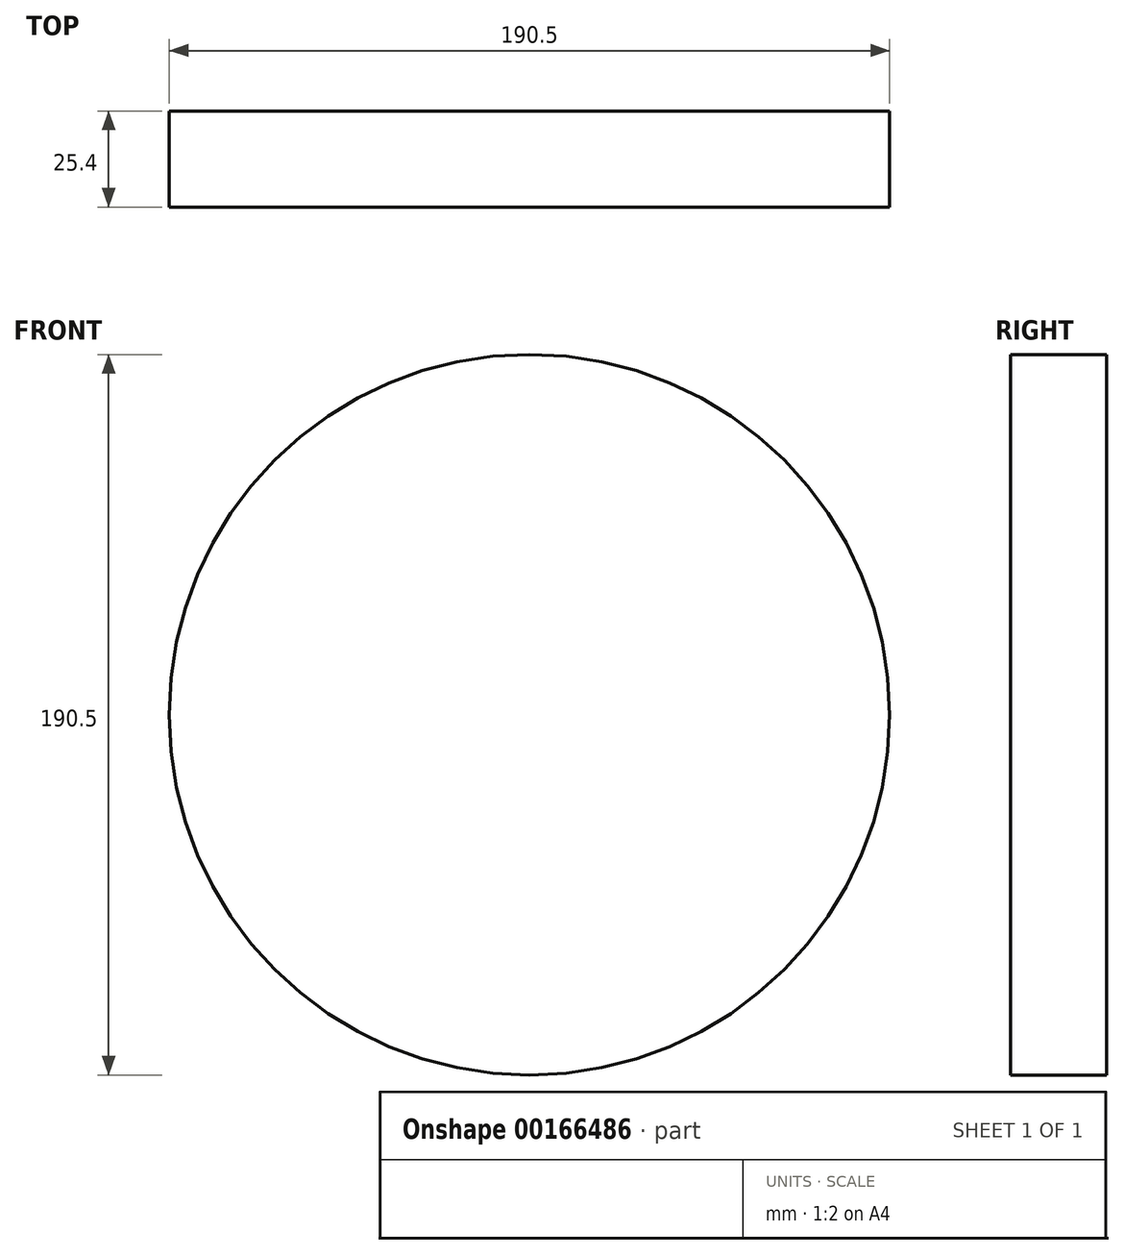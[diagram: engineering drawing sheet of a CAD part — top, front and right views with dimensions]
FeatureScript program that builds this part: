
annotation { "Feature Type Name" : "Feature", "Feature Type Description" : "" }
export const myFeature = defineFeature(function(context is Context, id is Id, definition is map)
    precondition{}
    {
        {
            var Q0;
            Q0=qCreatedBy(makeId("Front.planeOp"),FACE);
            var sketch = newSketch(context, id + "F0", { "sketchPlane" : qUnion([Q0])});
            skCircle(sketch, "E0", {"center": v(0, 0) * mm, "radius": 95.25 * mm});
            skSolve(sketch);
        }
        {
            var Q0;
            Q0 = qSketchRegion(id + "F0", true);
            extrude(context, id + "F1", {"entities" : qUnion([Q0]), "depth" : 25.4 * mm});
        }
    });
